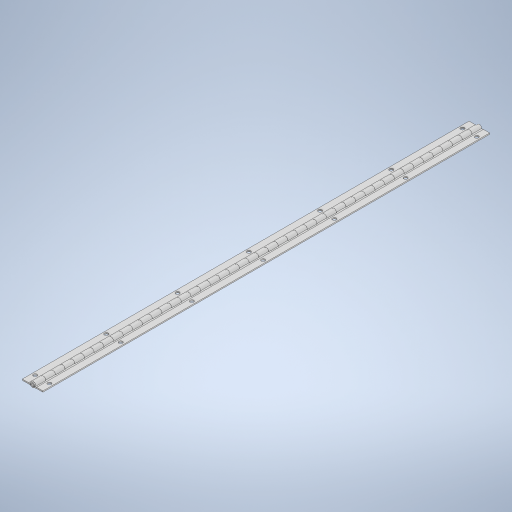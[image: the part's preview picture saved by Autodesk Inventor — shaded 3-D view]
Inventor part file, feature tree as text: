
AUTODESK INVENTOR PART (.ipt)
format: ipt  version: 2023 (Build 270158000, 158)  size: 609,792 bytes
history: native  units: in
note: dims shown in document units (in); Inventor stores cm internally (conversion verified against a paired STEP export)
features: extrude x2, sketch x2, other x2, hole x1, pattern_linear x1
ambient origin geometry x8: Origin, YZ Plane, XZ Plane, XY Plane, X Axis, Y Axis, Z Axis, Center Point
bodies: Solid1 (feature_tree), Solid2 (feature_tree), Solid3 (feature_tree)
feature tree (8):
  extrude  "Extrusion2"  TaperAngle=0.0deg  [1 undecoded]
  hole  "Hole1"  [1 undecoded]
  pattern_linear  "Rectangular Pattern1"  Spacing1=0.7385in  [1 undecoded]
  sketch  "Sketch2"  dims[d2=12.9469in d3=0.0in d4=0.0in]
  sketch  "Sketch3"  dims[d5=0.194in d6=0.75in d7=0.375in d8=0.25in d9=0.5635in d10=1.0in d11=0.8108in d13=0.162in d15=0.7385in d16=0.5in d17=2.7559in d19=3.6755in]
  other  "LPattern1"
  other  "LPattern2"
  extrude  "Extrude5"  Depth=0.5in
note: 3 required parameter values undecoded (feature->parameter linkage not recoverable at this tier; creation-order binding heuristic only, values carry confidence <= 0.55)
